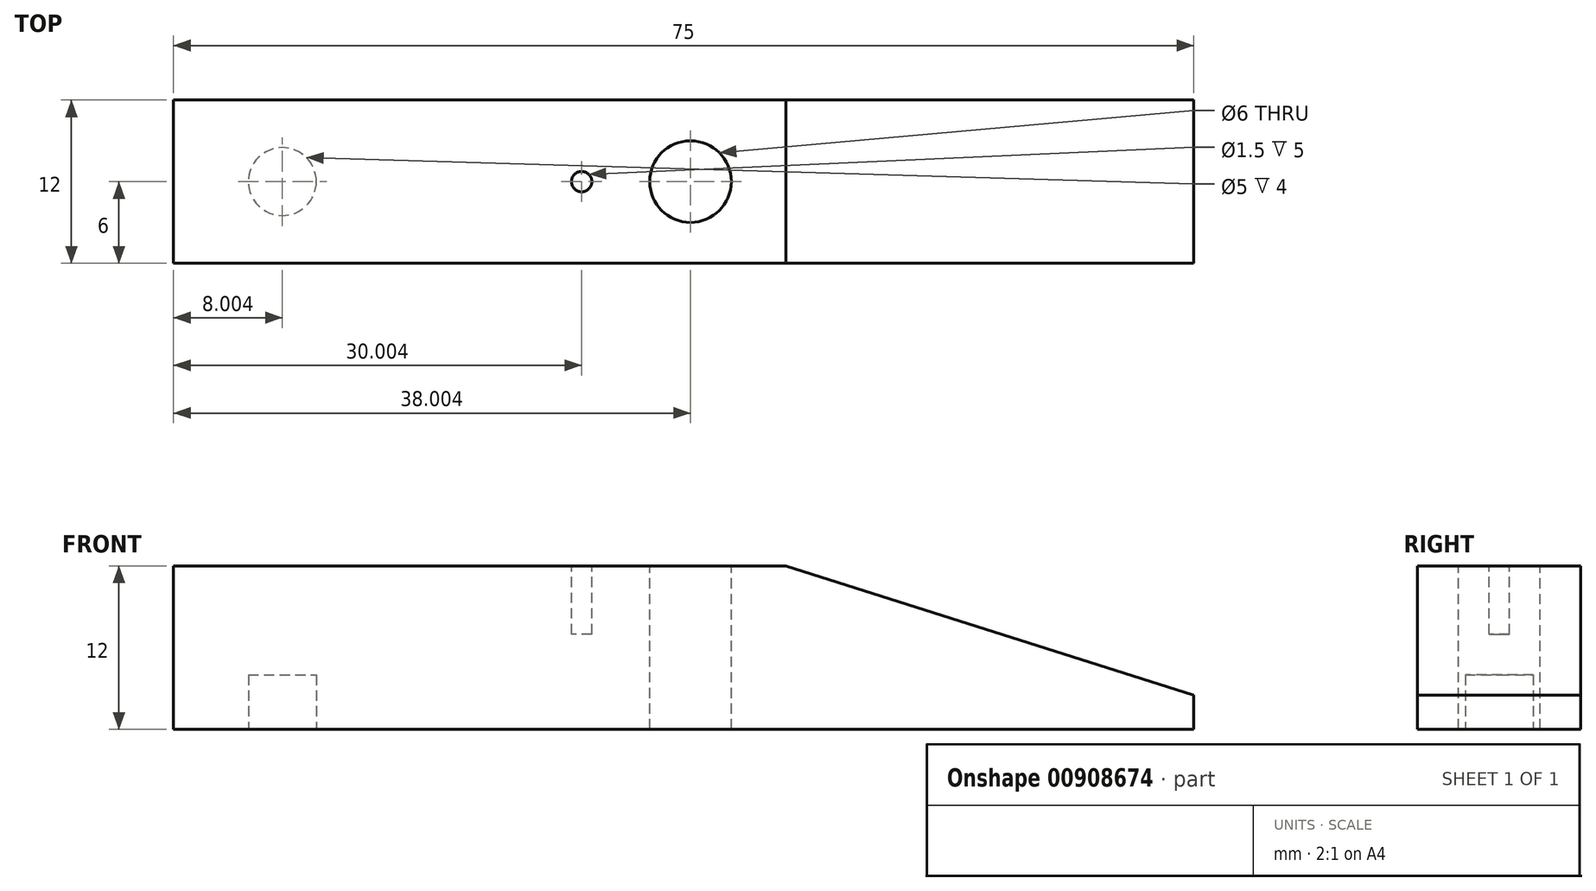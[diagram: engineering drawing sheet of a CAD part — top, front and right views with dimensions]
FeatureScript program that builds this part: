
annotation { "Feature Type Name" : "Feature", "Feature Type Description" : "" }
export const myFeature = defineFeature(function(context is Context, id is Id, definition is map)
    precondition{}
    {
        {
            var Q0;
            Q0=qCreatedBy(makeId("Front.planeOp"),FACE);
            var sketch = newSketch(context, id + "F0", { "sketchPlane" : qUnion([Q0])});
            skLineSegment(sketch, "E0", {"start": v(-17.52, -0.72) * mm, "end": v(27.48, -0.72) * mm});
            skLineSegment(sketch, "E1", {"start": v(27.48, -0.72) * mm, "end": v(57.48, -10.22) * mm});
            skLineSegment(sketch, "E2", {"start": v(57.48, -10.22) * mm, "end": v(57.48, -12.72) * mm});
            skLineSegment(sketch, "E3", {"start": v(57.48, -12.72) * mm, "end": v(-17.52, -12.72) * mm});
            skLineSegment(sketch, "E4", {"start": v(-17.52, -12.72) * mm, "end": v(-17.52, -0.72) * mm});
            skSolve(sketch);
        }
        {
            var Q0;
            Q0 = qSketchRegion(id + "F0", true);
            extrude(context, id + "F1", {"entities" : qUnion([Q0]), "depth" : 12 * mm, "offsetDistance" : 25 * mm});
        }
        {
            var Q0;
            Q0=makeQuery(id+"F1.opExtrude","SWEPT_FACE",FACE,{"disambiguationData":[OSD([sQuery(id+"F0.wireOp",EDGE,"E0")])]});
            var sketch = newSketch(context, id + "F2", { "sketchPlane" : qUnion([Q0])});
            skCircle(sketch, "E5", {"center": v(20.48, -6) * mm, "radius": 3 * mm});
            skSolve(sketch);
        }
        {
            var Q0;
            Q0 = qSketchRegion(id + "F2", true);
            extrude(context, id + "F3", {"entities" : qUnion([Q0]), "operationType" : NewBodyOperationType.REMOVE, "endBound" : BoundingType.THROUGH_ALL, "oppositeDirection" : true, "depth" : 25 * mm, "offsetDistance" : 25 * mm});
        }
        {
            var Q0;
            Q0=makeQuery(id+"F1.opExtrude","SWEPT_FACE",FACE,{"disambiguationData":[OSD([sQuery(id+"F0.wireOp",EDGE,"E0")])]});
            var sketch = newSketch(context, id + "F4", { "sketchPlane" : qUnion([Q0])});
            skCircle(sketch, "E6", {"center": v(12.48, -6) * mm, "radius": 0.75 * mm});
            skSolve(sketch);
        }
        {
            var Q0;
            Q0 = qSketchRegion(id + "F4", true);
            extrude(context, id + "F5", {"entities" : qUnion([Q0]), "operationType" : NewBodyOperationType.REMOVE, "oppositeDirection" : true, "depth" : 5 * mm, "offsetDistance" : 25 * mm});
        }
        {
            var Q0;
            Q0=makeQuery(id+"F1.opExtrude","SWEPT_FACE",FACE,{"disambiguationData":[OSD([sQuery(id+"F0.wireOp",EDGE,"E3")])]});
            var sketch = newSketch(context, id + "F6", { "sketchPlane" : qUnion([Q0])});
            skCircle(sketch, "E7", {"center": v(-9.52, 6) * mm, "radius": 2.5 * mm});
            skSolve(sketch);
        }
        {
            var Q0;
            Q0 = qSketchRegion(id + "F6", true);
            extrude(context, id + "F7", {"entities" : qUnion([Q0]), "operationType" : NewBodyOperationType.REMOVE, "oppositeDirection" : true, "depth" : 4 * mm, "offsetDistance" : 25 * mm});
        }
    });
